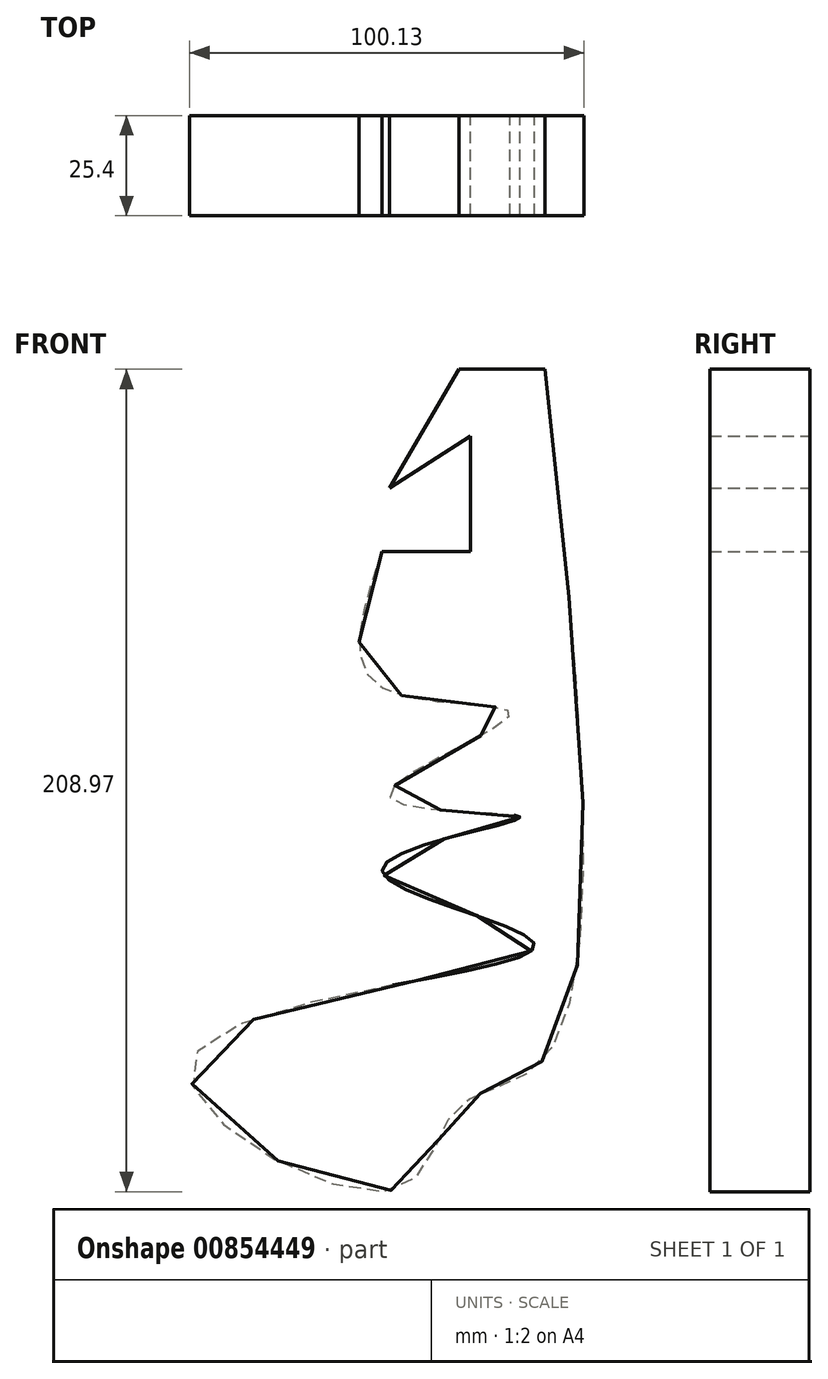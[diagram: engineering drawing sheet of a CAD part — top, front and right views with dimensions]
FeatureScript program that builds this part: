
annotation { "Feature Type Name" : "Feature", "Feature Type Description" : "" }
export const myFeature = defineFeature(function(context is Context, id is Id, definition is map)
    precondition{}
    {
        {
            var Q0;
            Q0=qCreatedBy(makeId("Front.planeOp"),FACE);
            var sketch = newSketch(context, id + "F0", { "sketchPlane" : qUnion([Q0])});
            skLineSegment(sketch, "E0", {"start": v(-16.52, 60.56) * mm, "end": v(-38.36, 60.56) * mm});
            skLineSegment(sketch, "E1", {"start": v(-38.36, 60.56) * mm, "end": v(-56.03, 30.36) * mm});
            skLineSegment(sketch, "E2", {"start": v(-56.03, 30.36) * mm, "end": v(-35.47, 43.53) * mm});
            skLineSegment(sketch, "E3", {"start": v(-35.47, 43.53) * mm, "end": v(-35.47, 14.19) * mm});
            skLineSegment(sketch, "E4", {"start": v(-35.47, 14.19) * mm, "end": v(-57.94, 14.19) * mm});
            skFitSpline(sketch, "E5", {"points": [v(-57.94, 14.19) * mm, v(-57.94, -20.33) * mm, v(-25.5, -27.35) * mm, v(-56.03, -48.04) * mm, v(-22.91, -53.22) * mm, v(-57.94, -66.52) * mm, v(-19.22, -85.74) * mm, v(-106.06, -114.56) * mm, v(-56.03, -148.19) * mm, v(-39.17, -127.5) * mm, v(-16.63, -114.56) * mm, v(-16.52, 60.56) * mm], "startDerivative": vector(-197.09, -565.33) * mm, "endDerivative": vector(-149.36, 1353.15) * mm});
            skSolve(sketch);
        }
        {
            var Q0;
            Q0=makeQuery(id+"F0.imprint","IMPRINT",FACE,{"disambiguationData":[TD([[makeQuery(id+"F0.imprint","IMPRINT",EDGE,{"derivedFrom":sQuery(id+"F0.wireOp",EDGE,"E0")}),1.0]])]});
            extrude(context, id + "F1", {"entities" : qUnion([Q0]), "depth" : 25.4 * mm, "offsetDistance" : 25.4 * mm});
        }
    });
